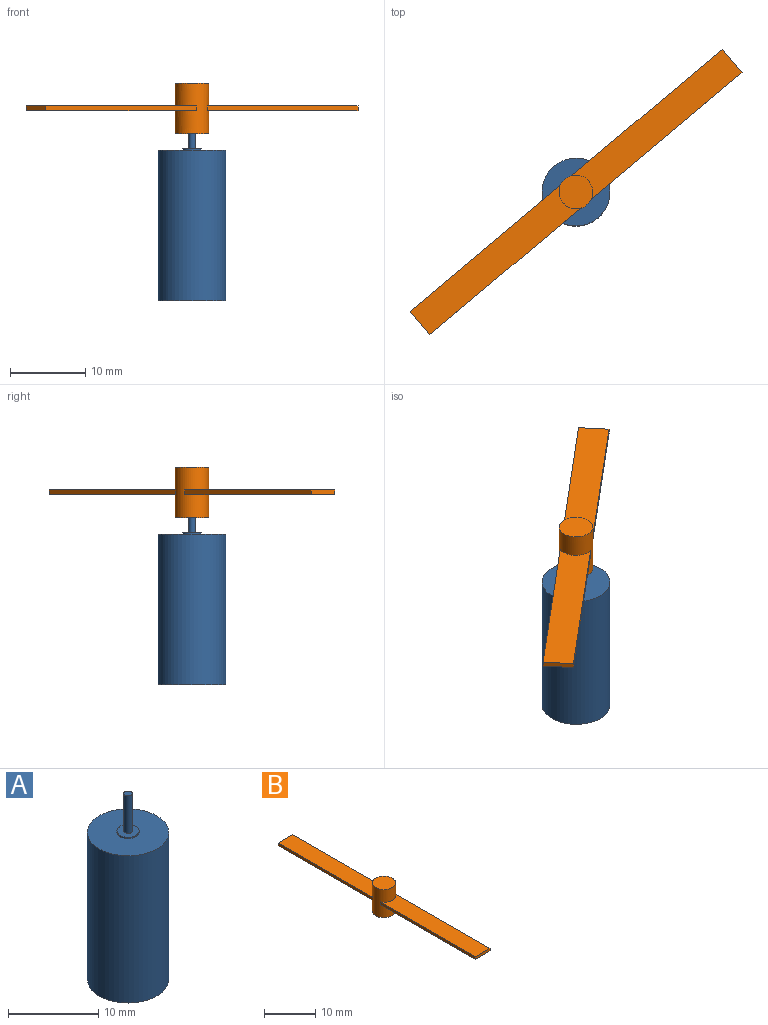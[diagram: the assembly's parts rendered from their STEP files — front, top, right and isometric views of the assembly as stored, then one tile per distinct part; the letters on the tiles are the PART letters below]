
ASSEMBLY  parts=2 mates=1
PART A: 7 faces, bbox 9x9x25.3 mm
  f0: cylinder r=4.51mm len=19.99mm, axis (0,0,-1), area 566.3mm2, adj f1,f2
  f1: plane 9.02x9.02mm, normal (0,0,1), area 59.1mm2, adj f0,f3
  f2: plane 9.02x9.02mm, normal (0,0,-1), area 63.9mm2, adj f0
  f3: cylinder r=1.22mm len=2.45mm, axis (0,0,-1), area 1.5mm2, adj f1,f4
  f4: plane 2.45x2.45mm, normal (0,0,1), area 4mm2, adj f3,f5
  f5: cylinder r=0.47mm len=5.08mm, axis (0,0,-1), area 15.2mm2, adj f4,f6
  f6: plane 0.95x0.95mm, normal (0,0,1), area 0.7mm2, adj f5
PART B: 15 faces, bbox 4.5x54.2x6.7 mm
  f0: cylinder r=2.25mm len=6.7mm, axis (0,0,-1), area 88.2mm2, adj f1,f2,f3,f4,f5,f6,f8,f9
  f1: plane 4.5x4.5mm, normal (0,0,1), area 15.9mm2, adj f0
  f2: plane 4.5x4.5mm, normal (0,0,-1), area 8.8mm2, adj f0,f13
  f3: plane 26.14x0.63mm, normal (1,0,0), area 16.5mm2, adj f0,f5,f6,f7
  f4: plane 26.14x0.63mm, normal (-1,0,0), area 16.5mm2, adj f0,f5,f6,f7
  f5: plane 26.14x4.06mm, normal (0,0,-1), area 102.5mm2, adj f0,f3,f4,f7
  f6: plane 26.14x4.06mm, normal (0,0,1), area 102.5mm2, adj f0,f3,f4,f7
  f7: plane 4.06x0.63mm, normal (0,-1,0), area 2.6mm2, adj f3,f4,f5,f6
  f8: plane 26.14x0.63mm, normal (1,0,0), area 16.5mm2, adj f0,f10,f11,f12
  f9: plane 26.14x0.63mm, normal (-1,0,0), area 16.5mm2, adj f0,f10,f11,f12
  f10: plane 26.14x4.06mm, normal (0,0,-1), area 102.5mm2, adj f0,f8,f9,f12
  f11: plane 26.14x4.06mm, normal (0,0,1), area 102.5mm2, adj f0,f8,f9,f12
  f12: plane 4.06x0.63mm, normal (0,1,0), area 2.6mm2, adj f8,f9,f10,f11
  f13: cylinder r=1.5mm len=3.6mm, axis (0,0,-1), area 33.9mm2, adj f2,f14
  f14: plane 3x3mm, normal (0,0,-1), area 7.1mm2, adj f13
PLACE A t=(-0.04,-0.35,-7.47)mm
PLACE B rot(axis=(0,0,-1),50deg) t=(-0.04,-0.35,14.77)mm
MATE revolute B.f0 <-> A.f5  axis (0,0,-1) through (-0.04,-0.35,17.8)mm
